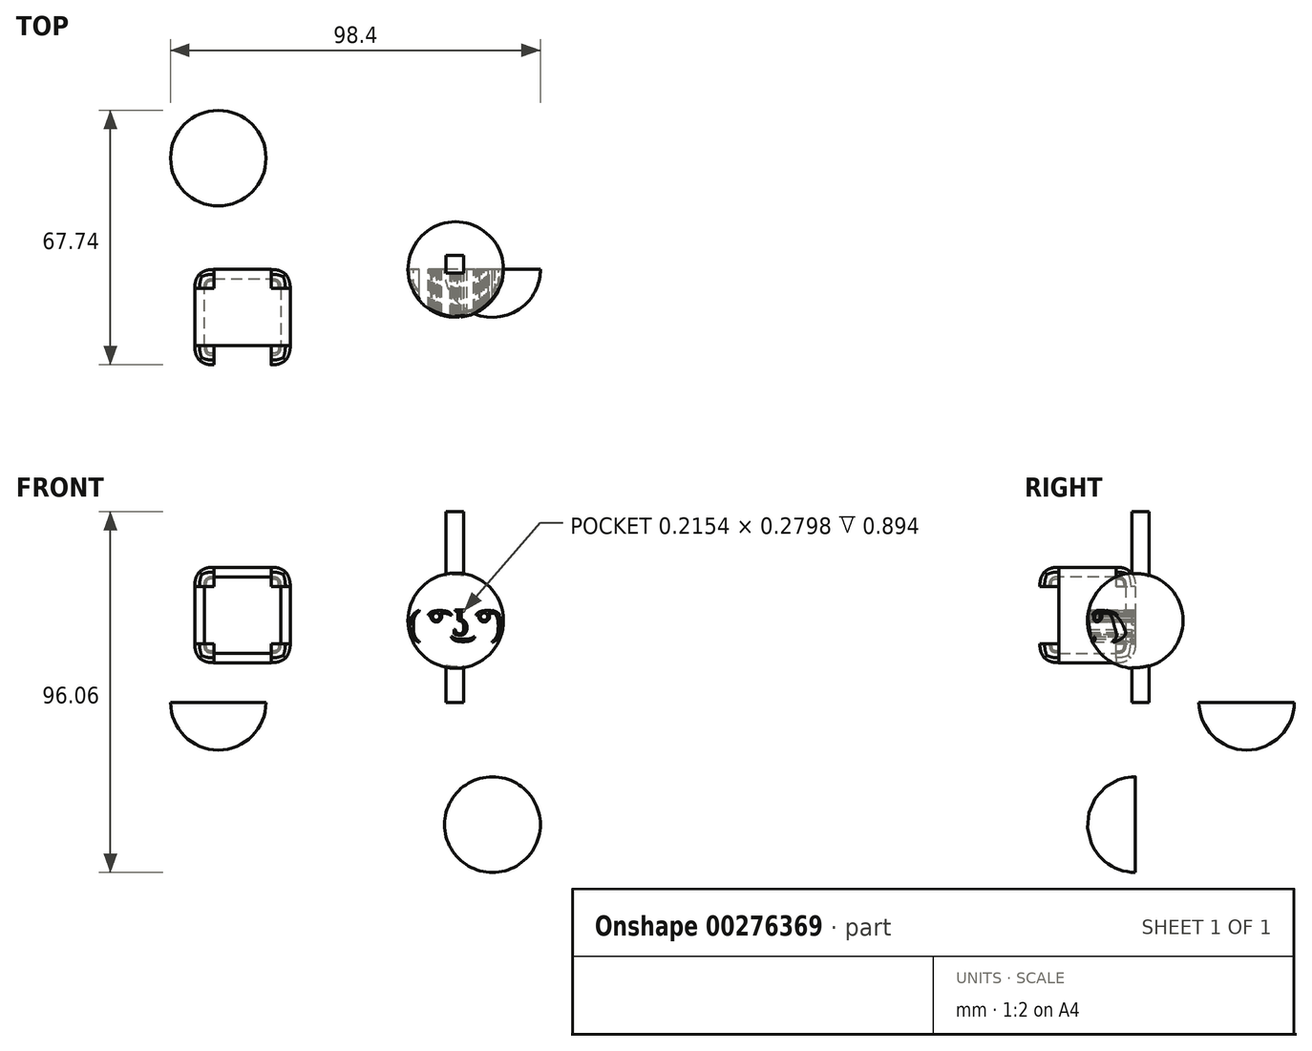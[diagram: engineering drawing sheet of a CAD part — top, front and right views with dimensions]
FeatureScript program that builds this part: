
annotation { "Feature Type Name" : "Feature", "Feature Type Description" : "" }
export const myFeature = defineFeature(function(context is Context, id is Id, definition is map)
    precondition{}
    {
        {
            var Q0;
            Q0=qCreatedBy(makeId("Front.planeOp"),FACE);
            var sketch = newSketch(context, id + "F0", { "sketchPlane" : qUnion([Q0])});
            skLineSegment(sketch, "E0.bottom", {"start": v(-44.93, 35.95) * mm, "end": v(-19.53, 35.95) * mm});
            skLineSegment(sketch, "E0.top", {"start": v(-44.93, 10.55) * mm, "end": v(-19.53, 10.55) * mm});
            skLineSegment(sketch, "E0.left", {"start": v(-44.93, 35.95) * mm, "end": v(-44.93, 10.55) * mm});
            skLineSegment(sketch, "E0.right", {"start": v(-19.53, 35.95) * mm, "end": v(-19.53, 10.55) * mm});
            skPoint(sketch, "E0.middle", {"position": v(-32.23, 23.25) * mm});
            skSolve(sketch);
        }
        {
            var Q0;
            Q0 = qSketchRegion(id + "F0", true);
            extrude(context, id + "F1", {"entities" : qUnion([Q0]), "depth" : 25.4 * mm});
        }
        {
            var Q0;
            Q0=makeQuery(id+"F1.opExtrude","CAP_FACE",FACE,{"disambiguationData":[OSD([sQuery(id+"F0.wireOp",EDGE,"E0.bottom"),sQuery(id+"F0.wireOp",EDGE,"E0.top"),sQuery(id+"F0.wireOp",EDGE,"E0.left"),sQuery(id+"F0.wireOp",EDGE,"E0.right")])],"isStart":false});
            var Q1;
            Q1=makeQuery(id+"F1.opExtrude","SWEPT_FACE",FACE,{"disambiguationData":[OSD([sQuery(id+"F0.wireOp",EDGE,"E0.top")])]});
            var Q2;
            Q2=makeQuery(id+"F1.opExtrude","SWEPT_FACE",FACE,{"disambiguationData":[OSD([sQuery(id+"F0.wireOp",EDGE,"E0.right")])]});
            var Q3;
            Q3=makeQuery(id+"F1.opExtrude","SWEPT_EDGE",EDGE,{"disambiguationData":[OSD([sQuery(id+"F0.wireOp",EDGE,"E0.bottom"),sQuery(id+"F0.wireOp",EDGE,"E0.left")])]});
            var Q4;
            Q4=makeQuery(id+"F1.opExtrude","CAP_EDGE",EDGE,{"disambiguationData":[OSD([sQuery(id+"F0.wireOp",EDGE,"E0.bottom")])],"isStart":true});
            var Q5;
            Q5=makeQuery(id+"F1.opExtrude","CAP_EDGE",EDGE,{"disambiguationData":[OSD([sQuery(id+"F0.wireOp",EDGE,"E0.left")])],"isStart":true});
            fillet(context, id + "F2", {"entities" : qUnion([Q0, Q1, Q2, Q3, Q4, Q5]), "radius" : 5.08 * mm, "tangentPropagation" : true, "rho" : 0.5, "crossSection" : FilletCrossSection.CONIC, "allowEdgeOverflow" : false});
        }
        {
            var Q0;
            Q0=qCreatedBy(makeId("Front.planeOp"),FACE);
            var sketch = newSketch(context, id + "F3", { "sketchPlane" : qUnion([Q0])});
            skLineSegment(sketch, "E1", {"start": v(24.5, 34.43) * mm, "end": v(24.5, 9.03) * mm});
            skArc(sketch, "E2", {"start": v(24.5, 9.03) * mm, "mid": v(37.2, 21.73) * mm, "end": v(24.5, 34.43) * mm});
            skSolve(sketch);
        }
        {
            var Q0;
            Q0 = qSketchRegion(id + "F3", true);
            var Q1;
            Q1=sQuery(id+"F3.wireOp",EDGE,"E1");
            revolve(context, id + "F4", {"entities" : qUnion([Q0]), "axis" : qUnion([Q1]), "revolveType" : RevolveType.FULL});
        }
        {
            var Q0;
            Q0=qCreatedBy(makeId("Top.planeOp"),FACE);
            var sketch = newSketch(context, id + "F5", { "sketchPlane" : qUnion([Q0])});
            skLineSegment(sketch, "E3", {"start": v(-38.67, 16.94) * mm, "end": v(-38.67, 42.34) * mm});
            skArc(sketch, "E4", {"start": v(-38.67, 16.94) * mm, "mid": v(-25.97, 29.64) * mm, "end": v(-38.67, 42.34) * mm});
            skSolve(sketch);
        }
        {
            var Q0;
            Q0 = qSketchRegion(id + "F5", true);
            var Q1;
            Q1=sQuery(id+"F5.wireOp",EDGE,"E3");
            revolve(context, id + "F6", {"entities" : qUnion([Q0]), "axis" : qUnion([Q1]), "revolveType" : RevolveType.ONE_DIRECTION, "angle" : 180 * degree});
        }
        {
            var Q0;
            Q0=qCreatedBy(makeId("Front.planeOp"),FACE);
            var sketch = newSketch(context, id + "F7", { "sketchPlane" : qUnion([Q0])});
            skLineSegment(sketch, "E5", {"start": v(34.28, -19.86) * mm, "end": v(34.28, -45.26) * mm});
            skArc(sketch, "E6", {"start": v(34.28, -45.26) * mm, "mid": v(47.03, -32.56) * mm, "end": v(34.28, -19.86) * mm});
            skSolve(sketch);
        }
        {
            var Q0;
            Q0=makeQuery(id+"F7.imprint","IMPRINT",FACE,{"disambiguationData":[TD([[makeQuery(id+"F7.imprint","IMPRINT",EDGE,{"derivedFrom":sQuery(id+"F7.wireOp",EDGE,"E5")}),1.0]])]});
            var Q1;
            Q1=sQuery(id+"F7.wireOp",EDGE,"E5");
            revolve(context, id + "F8", {"entities" : qUnion([Q0]), "axis" : qUnion([Q1]), "revolveType" : RevolveType.ONE_DIRECTION, "angle" : 180 * degree});
        }
        {
            var Q0;
            Q0=makeQuery(id+"F1.opExtrude","CAP_FACE",FACE,{"disambiguationData":[OSD([sQuery(id+"F0.wireOp",EDGE,"E0.bottom"),sQuery(id+"F0.wireOp",EDGE,"E0.top"),sQuery(id+"F0.wireOp",EDGE,"E0.left"),sQuery(id+"F0.wireOp",EDGE,"E0.right")])],"isStart":false});
            var Q1;
            {var subQ0=sQuery(id+"F0.wireOp",EDGE,"E0.bottom");Q1=makeQuery(id+"F2.opFillet","BLEND_FACE",FACE,{"disambiguationData":[OSD([subQ0]),TDD([makeQuery(id+"F1.opExtrude","CAP_EDGE",EDGE,{"disambiguationData":[OSD([subQ0])],"isStart":false})])]});}
            var Q2;
            {var subQ0=sQuery(id+"F0.wireOp",EDGE,"E0.top");Q2=makeQuery(id+"F2.opFillet","BLEND_FACE",FACE,{"disambiguationData":[OSD([subQ0]),TDD([makeQuery(id+"F1.opExtrude","CAP_EDGE",EDGE,{"disambiguationData":[OSD([subQ0])],"isStart":false})])]});}
            var Q3;
            {var subQ0=sQuery(id+"F0.wireOp",EDGE,"E0.right");Q3=makeQuery(id+"F2.opFillet","BLEND_FACE",FACE,{"disambiguationData":[OSD([subQ0]),TDD([makeQuery(id+"F1.opExtrude","CAP_EDGE",EDGE,{"disambiguationData":[OSD([subQ0])],"isStart":false})])]});}
            var Q4;
            {var subQ0=sQuery(id+"F0.wireOp",EDGE,"E0.left");Q4=makeQuery(id+"F2.opFillet","BLEND_FACE",FACE,{"disambiguationData":[OSD([subQ0]),TDD([makeQuery(id+"F1.opExtrude","CAP_EDGE",EDGE,{"disambiguationData":[OSD([subQ0])],"isStart":false})])]});}
            shell(context, id + "F9", {"entities" : qUnion([Q0, Q1, Q2, Q3, Q4]), "thickness" : 2.54 * mm});
        }
        {
            var Q0;
            Q0=qCreatedBy(makeId("Front.planeOp"),FACE);
            var sketch = newSketch(context, id + "F10", { "sketchPlane" : qUnion([Q0])});
            skText(sketch, "E7", { "text": "( ͡° ͜ʖ ͡°)", "fontName": "Tinos-Regular.ttf"});
            const initialGuessF10  = {"E7": [0.0119, 0.01795, 1, 0, 0.00683]};
            skSetInitialGuess(sketch, initialGuessF10);
            skSolve(sketch);
        }
        {
            var Q0;
            Q0 = qSketchRegion(id + "F10", true);
            var Q1;
            Q1 = qConstructionFilter(qBodyType(qCreatedBy(id + "F10" ,EDGE), BodyType.WIRE), ConstructionObject.NO);
            extrude(context, id + "F11", {"entities" : qUnion([Q0]), "operationType" : NewBodyOperationType.REMOVE, "surfaceEntities" : qUnion([Q1]), "depth" : 25.4 * mm});
        }
        {
            var Q0;
            Q0=qCreatedBy(makeId("Top.planeOp"),FACE);
            var sketch = newSketch(context, id + "F12", { "sketchPlane" : qUnion([Q0])});
            skLineSegment(sketch, "E8.bottom", {"start": v(21.26, 4.62) * mm, "end": v(21.07, 4.62) * mm});
            skLineSegment(sketch, "E8.top", {"start": v(21.26, -1.36) * mm, "end": v(21.07, -1.36) * mm});
            skLineSegment(sketch, "E9.bottom", {"start": v(21.96, 3.73) * mm, "end": v(26.57, 3.73) * mm});
            skLineSegment(sketch, "E9.top", {"start": v(21.96, -0.9) * mm, "end": v(26.57, -0.9) * mm});
            skLineSegment(sketch, "E9.left", {"start": v(21.96, 3.73) * mm, "end": v(21.96, -0.9) * mm});
            skLineSegment(sketch, "E9.right", {"start": v(26.57, 3.73) * mm, "end": v(26.57, -0.9) * mm});
            skSolve(sketch);
        }
        {
            var Q0;
            Q0 = qSketchRegion(id + "F12", true);
            extrude(context, id + "F13", {"entities" : qUnion([Q0]), "operationType" : NewBodyOperationType.ADD, "depth" : 50.8 * mm});
        }
    });
